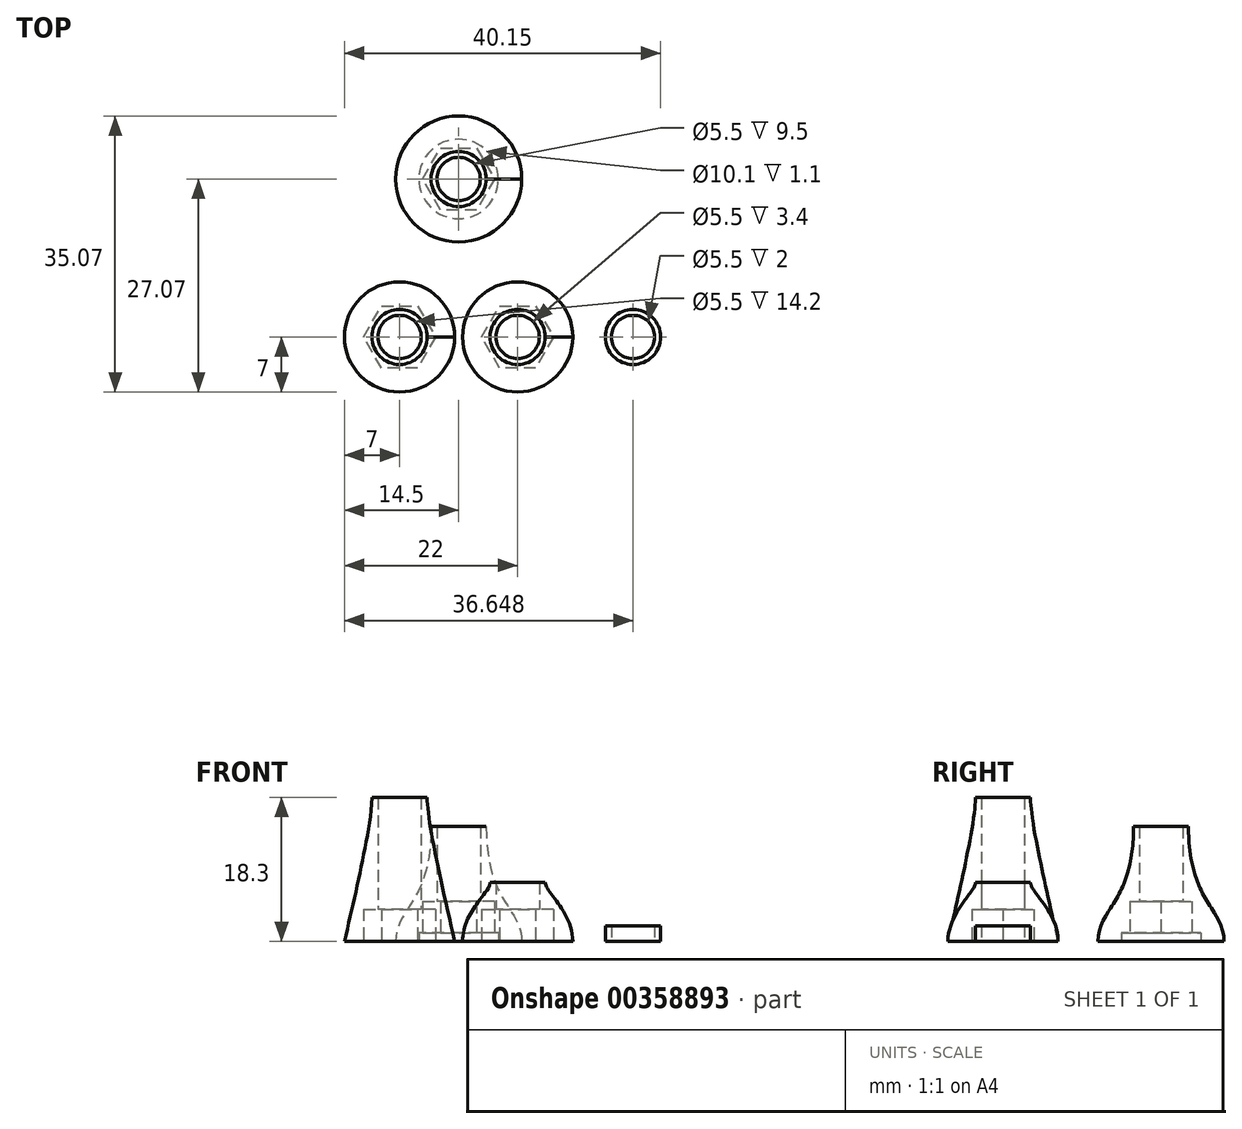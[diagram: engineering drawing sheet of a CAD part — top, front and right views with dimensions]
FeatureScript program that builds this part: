
annotation { "Feature Type Name" : "Feature", "Feature Type Description" : "" }
export const myFeature = defineFeature(function(context is Context, id is Id, definition is map)
    precondition{}
    {
        {
            var Q0;
            Q0=qCreatedBy(makeId("Top.planeOp"),FACE);
            var sketch = newSketch(context, id + "F0", { "sketchPlane" : qUnion([Q0])});
            skCircle(sketch, "E0", {"center": v(0, 0) * mm, "radius": 7 * mm});
            skCircle(sketch, "E1.1.0.1", {"center": v(15, 0) * mm, "radius": 7 * mm});
            skLineSegment(sketch, "E1.direction1", {"start": v(0, 0) * mm, "end": v(15, 0) * mm, "construction": true});
            skCircle(sketch, "E2", {"center": v(7.5, 20.07) * mm, "radius": 8 * mm});
            skCircle(sketch, "E3", {"center": v(29.65, 0) * mm, "radius": 3.5 * mm});
            skSolve(sketch);
        }
        {
            var Q0;
            Q0=qCreatedBy(makeId("Top.planeOp"),FACE);
            cPlane(context, id + "F1", {"entities" : qUnion([Q0]), "cplaneType" : CPlaneType.OFFSET, "offset" : 14.6 * mm, "width" : 150 * mm, "height" : 150 * mm});
        }
        {
            var Q0;
            Q0=qCreatedBy(id+"F1.planeOp",FACE);
            var sketch = newSketch(context, id + "F2", { "sketchPlane" : qUnion([Q0])});
            skCircle(sketch, "E4", {"center": v(7.5, 20.07) * mm, "radius": 3.5 * mm});
            skSolve(sketch);
        }
        {
            var Q0;
            Q0=makeQuery(id+"F2.imprint","IMPRINT",FACE,{"disambiguationData":[TD([[makeQuery(id+"F2.imprint","IMPRINT",EDGE,{"derivedFrom":sQuery(id+"F2.wireOp",EDGE,"E4")}),1.0]])]});
            var Q1;
            Q1=makeQuery(id+"F0.imprint","IMPRINT",FACE,{"disambiguationData":[TD([[makeQuery(id+"F0.imprint","IMPRINT",EDGE,{"derivedFrom":sQuery(id+"F0.wireOp",EDGE,"E2")}),1.0]])]});
            loft(context, id + "F3", {"sheetProfilesArray" : [{ "sheetProfileEntities" : qUnion([Q0]) }, { "sheetProfileEntities" : qUnion([Q1]) }], "startCondition" : LoftEndDerivativeType.NORMAL_TO_PROFILE, "startMagnitude" : 2, "endCondition" : LoftEndDerivativeType.NORMAL_TO_PROFILE, "endMagnitude" : 0.9});
        }
        {
            var Q0;
            Q0=qCreatedBy(makeId("Top.planeOp"),FACE);
            cPlane(context, id + "F4", {"entities" : qUnion([Q0]), "cplaneType" : CPlaneType.OFFSET, "offset" : 18.3 * mm, "width" : 150 * mm, "height" : 150 * mm});
        }
        {
            var Q0;
            Q0=qCreatedBy(id+"F4.planeOp",FACE);
            var sketch = newSketch(context, id + "F5", { "sketchPlane" : qUnion([Q0])});
            skCircle(sketch, "E5", {"center": v(0, 0) * mm, "radius": 3.5 * mm});
            skSolve(sketch);
        }
        {
            var Q0;
            Q0=makeQuery(id+"F0.imprint","IMPRINT",FACE,{"disambiguationData":[TD([[makeQuery(id+"F0.imprint","IMPRINT",EDGE,{"derivedFrom":sQuery(id+"F0.wireOp",EDGE,"E0")}),1.0]])]});
            var Q1;
            Q1=makeQuery(id+"F5.imprint","IMPRINT",FACE,{"disambiguationData":[TD([[makeQuery(id+"F5.imprint","IMPRINT",EDGE,{"derivedFrom":sQuery(id+"F5.wireOp",EDGE,"E5")}),1.0]])]});
            loft(context, id + "F6", {"sheetProfilesArray" : [{ "sheetProfileEntities" : qUnion([Q0]) }, { "sheetProfileEntities" : qUnion([Q1]) }], "endCondition" : LoftEndDerivativeType.NORMAL_TO_PROFILE, "endMagnitude" : 0.5});
        }
        {
            var Q0;
            Q0=qCreatedBy(makeId("Top.planeOp"),FACE);
            cPlane(context, id + "F7", {"entities" : qUnion([Q0]), "cplaneType" : CPlaneType.OFFSET, "offset" : 7.5 * mm, "width" : 150 * mm, "height" : 150 * mm});
        }
        {
            var Q0;
            Q0=qCreatedBy(id+"F7.planeOp",FACE);
            var sketch = newSketch(context, id + "F8", { "sketchPlane" : qUnion([Q0])});
            skCircle(sketch, "E6", {"center": v(15, 0) * mm, "radius": 3.5 * mm});
            skSolve(sketch);
        }
        {
            var Q0;
            Q0=makeQuery(id+"F0.imprint","IMPRINT",FACE,{"disambiguationData":[TD([[makeQuery(id+"F0.imprint","IMPRINT",EDGE,{"derivedFrom":sQuery(id+"F0.wireOp",EDGE,"E1.1.0.1")}),1.0]])]});
            var Q1;
            Q1=makeQuery(id+"F8.imprint","IMPRINT",FACE,{"disambiguationData":[TD([[makeQuery(id+"F8.imprint","IMPRINT",EDGE,{"derivedFrom":sQuery(id+"F8.wireOp",EDGE,"E6")}),1.0]])]});
            loft(context, id + "F9", {"sheetProfilesArray" : [{ "sheetProfileEntities" : qUnion([Q0]) }, { "sheetProfileEntities" : qUnion([Q1]) }], "startCondition" : LoftEndDerivativeType.NORMAL_TO_PROFILE, "startMagnitude" : 1.5, "endCondition" : LoftEndDerivativeType.NORMAL_TO_PROFILE, "endMagnitude" : 0.5});
        }
        {
            var Q0;
            Q0=makeQuery(id+"F0.imprint","IMPRINT",FACE,{"disambiguationData":[TD([[makeQuery(id+"F0.imprint","IMPRINT",EDGE,{"derivedFrom":sQuery(id+"F0.wireOp",EDGE,"E3")}),1.0]])]});
            extrude(context, id + "F10", {"entities" : qUnion([Q0]), "depth" : 2 * mm, "offsetDistance" : 25 * mm});
        }
        {
            var Q0;
            Q0=qCreatedBy(makeId("Top.planeOp"),FACE);
            var sketch = newSketch(context, id + "F11", { "sketchPlane" : qUnion([Q0])});
            skCircle(sketch, "E7", {"center": v(0, 0) * mm, "radius": 2.75 * mm});
            skCircle(sketch, "E8", {"center": v(7.5, 20.07) * mm, "radius": 2.75 * mm});
            skCircle(sketch, "E9", {"center": v(15, 0) * mm, "radius": 2.75 * mm});
            skCircle(sketch, "E10", {"center": v(29.65, 0) * mm, "radius": 2.75 * mm});
            skSolve(sketch);
        }
        {
            var Q0;
            Q0 = qSketchRegion(id + "F11", true);
            extrude(context, id + "F12", {"entities" : qUnion([Q0]), "operationType" : NewBodyOperationType.REMOVE, "endBound" : BoundingType.THROUGH_ALL, "depth" : 25 * mm, "offsetDistance" : 25 * mm});
        }
        {
            var Q0;
            Q0=qCreatedBy(makeId("Top.planeOp"),FACE);
            var sketch = newSketch(context, id + "F13", { "sketchPlane" : qUnion([Q0])});
            skCircle(sketch, "E11.cCircle", {"center": v(0, 0) * mm, "radius": 3.95 * mm, "construction": true});
            skLineSegment(sketch, "E11.0", {"start": v(-2.28, 3.95) * mm, "end": v(2.28, 3.95) * mm});
            skLineSegment(sketch, "E11.1", {"start": v(2.28, 3.95) * mm, "end": v(4.56, 0) * mm});
            skLineSegment(sketch, "E11.2", {"start": v(4.56, 0) * mm, "end": v(2.28, -3.95) * mm});
            skLineSegment(sketch, "E11.3", {"start": v(2.28, -3.95) * mm, "end": v(-2.28, -3.95) * mm});
            skLineSegment(sketch, "E11.4", {"start": v(-2.28, -3.95) * mm, "end": v(-4.56, 0) * mm});
            skLineSegment(sketch, "E11.5", {"start": v(-4.56, 0) * mm, "end": v(-2.28, 3.95) * mm});
            skPoint(sketch, "E11.0.midPoint", {"position": v(0, 3.95) * mm});
            skCircle(sketch, "E12.cCircle", {"center": v(15, 0) * mm, "radius": 3.95 * mm, "construction": true});
            skLineSegment(sketch, "E12.0", {"start": v(12.72, 3.95) * mm, "end": v(17.28, 3.95) * mm});
            skLineSegment(sketch, "E12.1", {"start": v(17.28, 3.95) * mm, "end": v(19.56, 0) * mm});
            skLineSegment(sketch, "E12.2", {"start": v(19.56, 0) * mm, "end": v(17.28, -3.95) * mm});
            skLineSegment(sketch, "E12.3", {"start": v(17.28, -3.95) * mm, "end": v(12.72, -3.95) * mm});
            skLineSegment(sketch, "E12.4", {"start": v(12.72, -3.95) * mm, "end": v(10.44, 0) * mm});
            skLineSegment(sketch, "E12.5", {"start": v(10.44, 0) * mm, "end": v(12.72, 3.95) * mm});
            skPoint(sketch, "E12.0.midPoint", {"position": v(15, 3.95) * mm});
            skCircle(sketch, "E13.cCircle", {"center": v(7.5, 20.07) * mm, "radius": 3.95 * mm, "construction": true});
            skLineSegment(sketch, "E13.0", {"start": v(5.22, 24.02) * mm, "end": v(9.78, 24.02) * mm});
            skLineSegment(sketch, "E13.1", {"start": v(9.78, 24.02) * mm, "end": v(12.06, 20.07) * mm});
            skLineSegment(sketch, "E13.2", {"start": v(12.06, 20.07) * mm, "end": v(9.78, 16.12) * mm});
            skLineSegment(sketch, "E13.3", {"start": v(9.78, 16.12) * mm, "end": v(5.22, 16.12) * mm});
            skLineSegment(sketch, "E13.4", {"start": v(5.22, 16.12) * mm, "end": v(2.94, 20.07) * mm});
            skLineSegment(sketch, "E13.5", {"start": v(2.94, 20.07) * mm, "end": v(5.22, 24.02) * mm});
            skPoint(sketch, "E13.0.midPoint", {"position": v(7.5, 24.02) * mm});
            skCircle(sketch, "E14", {"center": v(7.5, 20.07) * mm, "radius": 5.05 * mm});
            skSolve(sketch);
        }
        {
            var Q0;
            Q0=makeQuery(id+"F13.imprint","IMPRINT",FACE,{"disambiguationData":[TD([[makeQuery(id+"F13.imprint","IMPRINT",EDGE,{"derivedFrom":sQuery(id+"F13.wireOp",EDGE,"E11.0")}),-1.0]])]});
            var Q1;
            Q1=makeQuery(id+"F13.imprint","IMPRINT",FACE,{"disambiguationData":[TD([[makeQuery(id+"F13.imprint","IMPRINT",EDGE,{"derivedFrom":sQuery(id+"F13.wireOp",EDGE,"E12.0")}),-1.0]])]});
            extrude(context, id + "F14", {"entities" : qUnion([Q0, Q1]), "operationType" : NewBodyOperationType.REMOVE, "depth" : 4.1 * mm, "offsetDistance" : 25 * mm});
        }
        {
            var Q0;
            Q0=makeQuery(id+"F13.imprint","IMPRINT",FACE,{"disambiguationData":[TD([[makeQuery(id+"F13.imprint","IMPRINT",EDGE,{"derivedFrom":sQuery(id+"F13.wireOp",EDGE,"E13.0")}),-1.0]])]});
            extrude(context, id + "F15", {"entities" : qUnion([Q0]), "operationType" : NewBodyOperationType.REMOVE, "depth" : 5.1 * mm, "offsetDistance" : 25 * mm});
        }
        {
            var Q0;
            Q0=makeQuery(id+"F13.imprint","IMPRINT",FACE,{"disambiguationData":[TD([[makeQuery(id+"F13.imprint","IMPRINT",EDGE,{"derivedFrom":sQuery(id+"F13.wireOp",EDGE,"E13.0")}),1.0]])]});
            extrude(context, id + "F16", {"entities" : qUnion([Q0]), "operationType" : NewBodyOperationType.REMOVE, "depth" : 1.1 * mm, "offsetDistance" : 25 * mm});
        }
    });
